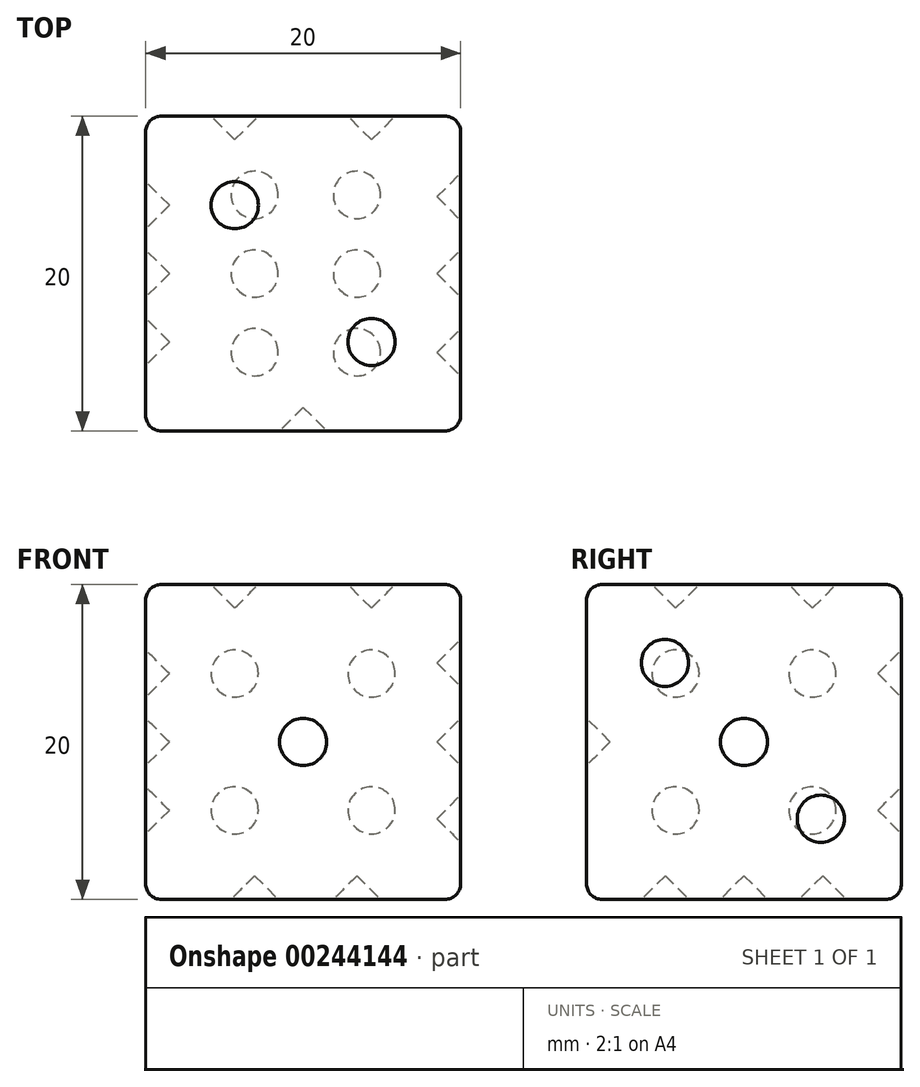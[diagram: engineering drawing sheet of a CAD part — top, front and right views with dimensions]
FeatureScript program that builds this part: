
annotation { "Feature Type Name" : "Feature", "Feature Type Description" : "" }
export const myFeature = defineFeature(function(context is Context, id is Id, definition is map)
    precondition{}
    {
        {
            var Q0;
            Q0=qCreatedBy(makeId("Top.planeOp"),FACE);
            var sketch = newSketch(context, id + "F0", { "sketchPlane" : qUnion([Q0])});
            skLineSegment(sketch, "E0.bottom", {"start": v(0, 0) * mm, "end": v(20, 0) * mm});
            skLineSegment(sketch, "E0.top", {"start": v(0, 20) * mm, "end": v(20, 20) * mm});
            skLineSegment(sketch, "E0.left", {"start": v(0, 0) * mm, "end": v(0, 20) * mm});
            skLineSegment(sketch, "E0.right", {"start": v(20, 0) * mm, "end": v(20, 20) * mm});
            skSolve(sketch);
        }
        {
            var Q0;
            Q0 = qSketchRegion(id + "F0", true);
            extrude(context, id + "F1", {"entities" : qUnion([Q0]), "depth" : 20 * mm});
        }
        {
            var Q0;
            Q0=makeQuery(id+"F1.opExtrude","SWEPT_FACE",FACE,{"disambiguationData":[OSD([sQuery(id+"F0.wireOp",EDGE,"E0.bottom")])]});
            var sketch = newSketch(context, id + "F2", { "sketchPlane" : qUnion([Q0])});
            skLineSegment(sketch, "E1", {"start": v(10, 20) * mm, "end": v(10, 0) * mm, "construction": true});
            skCircle(sketch, "E2", {"center": v(10, 10) * mm, "radius": 1.5 * mm});
            skSolve(sketch);
        }
        {
            var Q0;
            Q0 = qSketchRegion(id + "F2", true);
            extrude(context, id + "F3", {"entities" : qUnion([Q0]), "operationType" : NewBodyOperationType.REMOVE, "oppositeDirection" : true, "depth" : 1.5 * mm});
        }
        {
            var Q0;
            Q0=makeQuery(id+"F1.opExtrude","CAP_EDGE",EDGE,{"disambiguationData":[OSD([sQuery(id+"F0.wireOp",EDGE,"E0.left")])],"isStart":false});
            var Q1;
            Q1=makeQuery(id+"F1.opExtrude","CAP_EDGE",EDGE,{"disambiguationData":[OSD([sQuery(id+"F0.wireOp",EDGE,"E0.right")])],"isStart":false});
            var Q2;
            Q2=makeQuery(id+"F1.opExtrude","CAP_EDGE",EDGE,{"disambiguationData":[OSD([sQuery(id+"F0.wireOp",EDGE,"E0.right")])],"isStart":true});
            var Q3;
            Q3=makeQuery(id+"F1.opExtrude","CAP_EDGE",EDGE,{"disambiguationData":[OSD([sQuery(id+"F0.wireOp",EDGE,"E0.left")])],"isStart":true});
            var Q4;
            Q4=makeQuery(id+"F1.opExtrude","SWEPT_EDGE",EDGE,{"disambiguationData":[OSD([sQuery(id+"F0.wireOp",EDGE,"E0.bottom"),sQuery(id+"F0.wireOp",EDGE,"E0.left")])]});
            var Q5;
            Q5=makeQuery(id+"F1.opExtrude","SWEPT_EDGE",EDGE,{"disambiguationData":[OSD([sQuery(id+"F0.wireOp",EDGE,"E0.bottom"),sQuery(id+"F0.wireOp",EDGE,"E0.right")])]});
            var Q6;
            Q6=makeQuery(id+"F1.opExtrude","SWEPT_EDGE",EDGE,{"disambiguationData":[OSD([sQuery(id+"F0.wireOp",EDGE,"E0.top"),sQuery(id+"F0.wireOp",EDGE,"E0.right")])]});
            var Q7;
            Q7=makeQuery(id+"F1.opExtrude","CAP_EDGE",EDGE,{"disambiguationData":[OSD([sQuery(id+"F0.wireOp",EDGE,"E0.top")])],"isStart":false});
            var Q8;
            Q8=makeQuery(id+"F1.opExtrude","SWEPT_EDGE",EDGE,{"disambiguationData":[OSD([sQuery(id+"F0.wireOp",EDGE,"E0.top"),sQuery(id+"F0.wireOp",EDGE,"E0.left")])]});
            var Q9;
            Q9=makeQuery(id+"F1.opExtrude","CAP_EDGE",EDGE,{"disambiguationData":[OSD([sQuery(id+"F0.wireOp",EDGE,"E0.bottom")])],"isStart":true});
            var Q10;
            Q10=makeQuery(id+"F1.opExtrude","CAP_EDGE",EDGE,{"disambiguationData":[OSD([sQuery(id+"F0.wireOp",EDGE,"E0.top")])],"isStart":true});
            var Q11;
            Q11=makeQuery(id+"F1.opExtrude","SWEPT_FACE",FACE,{"disambiguationData":[OSD([sQuery(id+"F0.wireOp",EDGE,"E0.right")])]});
            var Q12;
            Q12=makeQuery(id+"F1.opExtrude","CAP_EDGE",EDGE,{"disambiguationData":[OSD([sQuery(id+"F0.wireOp",EDGE,"E0.bottom")])],"isStart":false});
            fillet(context, id + "F4", {"entities" : qUnion([Q0, Q1, Q2, Q3, Q4, Q5, Q6, Q7, Q8, Q9, Q10, Q11, Q12]), "radius" : 1 * mm, "tangentPropagation" : true, "allowEdgeOverflow" : false});
        }
        {
            var Q0;
            Q0=makeQuery(id+"F3.boolean.opBoolean","COPY",EDGE,{"derivedFrom":makeQuery(id+"F3.opExtrude","CAP_EDGE",EDGE,{"disambiguationData":[OSD([sQuery(id+"F2.wireOp",EDGE,"E2")])],"isStart":false})});
            chamfer(context, id + "F5", {"entities" : qUnion([Q0]), "width" : 1.5 * mm, "tangentPropagation" : true});
        }
        {
            var Q0;
            Q0=makeQuery(id+"F1.opExtrude","SWEPT_FACE",FACE,{"disambiguationData":[OSD([sQuery(id+"F0.wireOp",EDGE,"E0.right")])]});
            var sketch = newSketch(context, id + "F6", { "sketchPlane" : qUnion([Q0])});
            skCircle(sketch, "E3", {"center": v(4.98, 15.02) * mm, "radius": 1.5 * mm});
            skCircle(sketch, "E4", {"center": v(10, 10) * mm, "radius": 1.5 * mm});
            skCircle(sketch, "E5", {"center": v(14.88, 5.12) * mm, "radius": 1.5 * mm});
            skSolve(sketch);
        }
        {
            var Q0;
            Q0=makeQuery(id+"F1.opExtrude","SWEPT_FACE",FACE,{"disambiguationData":[OSD([sQuery(id+"F0.wireOp",EDGE,"E0.top")])]});
            var sketch = newSketch(context, id + "F7", { "sketchPlane" : qUnion([Q0])});
            skCircle(sketch, "E6", {"center": v(-14.34, 5.66) * mm, "radius": 1.5 * mm});
            skCircle(sketch, "E7", {"center": v(-5.66, 5.66) * mm, "radius": 1.5 * mm});
            skCircle(sketch, "E8", {"center": v(-5.66, 14.34) * mm, "radius": 1.5 * mm});
            skCircle(sketch, "E9", {"center": v(-14.34, 14.34) * mm, "radius": 1.5 * mm});
            skSolve(sketch);
        }
        {
            var Q0;
            Q0=makeQuery(id+"F1.opExtrude","CAP_FACE",FACE,{"disambiguationData":[OSD([sQuery(id+"F0.wireOp",EDGE,"E0.bottom"),sQuery(id+"F0.wireOp",EDGE,"E0.top"),sQuery(id+"F0.wireOp",EDGE,"E0.left"),sQuery(id+"F0.wireOp",EDGE,"E0.right")])],"isStart":true});
            var sketch = newSketch(context, id + "F8", { "sketchPlane" : qUnion([Q0])});
            skCircle(sketch, "E10", {"center": v(6.92, -5) * mm, "radius": 1.5 * mm});
            skCircle(sketch, "E11", {"center": v(6.92, -10) * mm, "radius": 1.5 * mm});
            skCircle(sketch, "E12", {"center": v(6.92, -15) * mm, "radius": 1.5 * mm});
            skCircle(sketch, "E13", {"center": v(13.41, -15) * mm, "radius": 1.5 * mm});
            skCircle(sketch, "E14", {"center": v(13.41, -10) * mm, "radius": 1.5 * mm});
            skCircle(sketch, "E15", {"center": v(13.41, -5) * mm, "radius": 1.5 * mm});
            skSolve(sketch);
        }
        {
            var Q0;
            Q0=makeQuery(id+"F1.opExtrude","SWEPT_FACE",FACE,{"disambiguationData":[OSD([sQuery(id+"F0.wireOp",EDGE,"E0.left")])]});
            var sketch = newSketch(context, id + "F9", { "sketchPlane" : qUnion([Q0])});
            skCircle(sketch, "E16", {"center": v(-10, 10) * mm, "radius": 1.5 * mm});
            skCircle(sketch, "E17", {"center": v(-14.34, 14.34) * mm, "radius": 1.5 * mm});
            skCircle(sketch, "E18", {"center": v(-14.34, 5.66) * mm, "radius": 1.5 * mm});
            skCircle(sketch, "E19", {"center": v(-5.66, 5.66) * mm, "radius": 1.5 * mm});
            skCircle(sketch, "E20", {"center": v(-5.66, 14.34) * mm, "radius": 1.5 * mm});
            skSolve(sketch);
        }
        {
            var Q0;
            Q0=makeQuery(id+"F9.imprint","IMPRINT",FACE,{"disambiguationData":[TD([[makeQuery(id+"F9.imprint","IMPRINT",EDGE,{"derivedFrom":sQuery(id+"F9.wireOp",EDGE,"E20")}),1.0]])]});
            var Q1;
            Q1=makeQuery(id+"F9.imprint","IMPRINT",FACE,{"disambiguationData":[TD([[makeQuery(id+"F9.imprint","IMPRINT",EDGE,{"derivedFrom":sQuery(id+"F9.wireOp",EDGE,"E16")}),1.0]])]});
            var Q2;
            Q2=makeQuery(id+"F9.imprint","IMPRINT",FACE,{"disambiguationData":[TD([[makeQuery(id+"F9.imprint","IMPRINT",EDGE,{"derivedFrom":sQuery(id+"F9.wireOp",EDGE,"E18")}),1.0]])]});
            var Q3;
            Q3=makeQuery(id+"F9.imprint","IMPRINT",FACE,{"disambiguationData":[TD([[makeQuery(id+"F9.imprint","IMPRINT",EDGE,{"derivedFrom":sQuery(id+"F9.wireOp",EDGE,"E19")}),1.0]])]});
            var Q4;
            Q4=makeQuery(id+"F9.imprint","IMPRINT",FACE,{"disambiguationData":[TD([[makeQuery(id+"F9.imprint","IMPRINT",EDGE,{"derivedFrom":sQuery(id+"F9.wireOp",EDGE,"E17")}),1.0]])]});
            var Q5;
            Q5=sQuery(id+"F9.wireOp",EDGE,"E19");
            var Q6;
            Q6=sQuery(id+"F9.wireOp",EDGE,"E16");
            var Q7;
            Q7=sQuery(id+"F9.wireOp",EDGE,"E18");
            var Q8;
            Q8=sQuery(id+"F9.wireOp",EDGE,"E17");
            var Q9;
            Q9=sQuery(id+"F9.wireOp",EDGE,"E20");
            extrude(context, id + "F10", {"entities" : qUnion([Q0, Q1, Q2, Q3, Q4]), "operationType" : NewBodyOperationType.REMOVE, "surfaceEntities" : qUnion([Q5, Q6, Q7, Q8, Q9]), "oppositeDirection" : true, "depth" : 1.5 * mm});
        }
        {
            var Q0;
            Q0=makeQuery(id+"F10.boolean.opBoolean","COPY",FACE,{"derivedFrom":makeQuery(id+"F10.opExtrude","CAP_FACE",FACE,{"disambiguationData":[OSD([sQuery(id+"F9.wireOp",EDGE,"E16")])],"isStart":false})});
            var Q1;
            Q1=makeQuery(id+"F10.boolean.opBoolean","COPY",FACE,{"derivedFrom":makeQuery(id+"F10.opExtrude","CAP_FACE",FACE,{"disambiguationData":[OSD([sQuery(id+"F9.wireOp",EDGE,"E18")])],"isStart":false})});
            var Q2;
            Q2=makeQuery(id+"F10.boolean.opBoolean","COPY",FACE,{"derivedFrom":makeQuery(id+"F10.opExtrude","CAP_FACE",FACE,{"disambiguationData":[OSD([sQuery(id+"F9.wireOp",EDGE,"E17")])],"isStart":false})});
            var Q3;
            Q3=makeQuery(id+"F10.boolean.opBoolean","COPY",FACE,{"derivedFrom":makeQuery(id+"F10.opExtrude","CAP_FACE",FACE,{"disambiguationData":[OSD([sQuery(id+"F9.wireOp",EDGE,"E20")])],"isStart":false})});
            var Q4;
            Q4=makeQuery(id+"F10.boolean.opBoolean","COPY",FACE,{"derivedFrom":makeQuery(id+"F10.opExtrude","CAP_FACE",FACE,{"disambiguationData":[OSD([sQuery(id+"F9.wireOp",EDGE,"E19")])],"isStart":false})});
            chamfer(context, id + "F11", {"entities" : qUnion([Q0, Q1, Q2, Q3, Q4]), "width" : 1.5 * mm, "tangentPropagation" : true});
        }
        {
            var Q0;
            Q0=makeQuery(id+"F8.imprint","IMPRINT",FACE,{"disambiguationData":[TD([[makeQuery(id+"F8.imprint","IMPRINT",EDGE,{"derivedFrom":sQuery(id+"F8.wireOp",EDGE,"E10")}),1.0]])]});
            var Q1;
            Q1=makeQuery(id+"F8.imprint","IMPRINT",FACE,{"disambiguationData":[TD([[makeQuery(id+"F8.imprint","IMPRINT",EDGE,{"derivedFrom":sQuery(id+"F8.wireOp",EDGE,"E15")}),1.0]])]});
            var Q2;
            Q2=makeQuery(id+"F8.imprint","IMPRINT",FACE,{"disambiguationData":[TD([[makeQuery(id+"F8.imprint","IMPRINT",EDGE,{"derivedFrom":sQuery(id+"F8.wireOp",EDGE,"E11")}),1.0]])]});
            var Q3;
            Q3=makeQuery(id+"F8.imprint","IMPRINT",FACE,{"disambiguationData":[TD([[makeQuery(id+"F8.imprint","IMPRINT",EDGE,{"derivedFrom":sQuery(id+"F8.wireOp",EDGE,"E14")}),1.0]])]});
            var Q4;
            Q4=makeQuery(id+"F8.imprint","IMPRINT",FACE,{"disambiguationData":[TD([[makeQuery(id+"F8.imprint","IMPRINT",EDGE,{"derivedFrom":sQuery(id+"F8.wireOp",EDGE,"E12")}),1.0]])]});
            var Q5;
            Q5=makeQuery(id+"F8.imprint","IMPRINT",FACE,{"disambiguationData":[TD([[makeQuery(id+"F8.imprint","IMPRINT",EDGE,{"derivedFrom":sQuery(id+"F8.wireOp",EDGE,"E13")}),1.0]])]});
            var Q6;
            Q6=sQuery(id+"F8.wireOp",EDGE,"E10");
            var Q7;
            Q7=sQuery(id+"F8.wireOp",EDGE,"E15");
            var Q8;
            Q8=sQuery(id+"F8.wireOp",EDGE,"E11");
            var Q9;
            Q9=sQuery(id+"F8.wireOp",EDGE,"E14");
            var Q10;
            Q10=sQuery(id+"F8.wireOp",EDGE,"E13");
            var Q11;
            Q11=sQuery(id+"F8.wireOp",EDGE,"E12");
            extrude(context, id + "F12", {"entities" : qUnion([Q0, Q1, Q2, Q3, Q4, Q5]), "operationType" : NewBodyOperationType.REMOVE, "surfaceEntities" : qUnion([Q6, Q7, Q8, Q9, Q10, Q11]), "oppositeDirection" : true, "depth" : 1.5 * mm});
        }
        {
            var Q0;
            Q0=makeQuery(id+"F12.boolean.opBoolean","COPY",FACE,{"derivedFrom":makeQuery(id+"F12.opExtrude","CAP_FACE",FACE,{"disambiguationData":[OSD([sQuery(id+"F8.wireOp",EDGE,"E10")])],"isStart":false})});
            var Q1;
            Q1=makeQuery(id+"F12.boolean.opBoolean","COPY",FACE,{"derivedFrom":makeQuery(id+"F12.opExtrude","CAP_FACE",FACE,{"disambiguationData":[OSD([sQuery(id+"F8.wireOp",EDGE,"E15")])],"isStart":false})});
            var Q2;
            Q2=makeQuery(id+"F12.boolean.opBoolean","COPY",FACE,{"derivedFrom":makeQuery(id+"F12.opExtrude","CAP_FACE",FACE,{"disambiguationData":[OSD([sQuery(id+"F8.wireOp",EDGE,"E11")])],"isStart":false})});
            var Q3;
            Q3=makeQuery(id+"F12.boolean.opBoolean","COPY",FACE,{"derivedFrom":makeQuery(id+"F12.opExtrude","CAP_FACE",FACE,{"disambiguationData":[OSD([sQuery(id+"F8.wireOp",EDGE,"E14")])],"isStart":false})});
            var Q4;
            Q4=makeQuery(id+"F12.boolean.opBoolean","COPY",FACE,{"derivedFrom":makeQuery(id+"F12.opExtrude","CAP_FACE",FACE,{"disambiguationData":[OSD([sQuery(id+"F8.wireOp",EDGE,"E13")])],"isStart":false})});
            var Q5;
            Q5=makeQuery(id+"F12.boolean.opBoolean","COPY",FACE,{"derivedFrom":makeQuery(id+"F12.opExtrude","CAP_FACE",FACE,{"disambiguationData":[OSD([sQuery(id+"F8.wireOp",EDGE,"E12")])],"isStart":false})});
            chamfer(context, id + "F13", {"entities" : qUnion([Q0, Q1, Q2, Q3, Q4, Q5]), "width" : 1.5 * mm, "tangentPropagation" : true});
        }
        {
            var Q0;
            Q0=makeQuery(id+"F6.imprint","IMPRINT",FACE,{"disambiguationData":[TD([[makeQuery(id+"F6.imprint","IMPRINT",EDGE,{"derivedFrom":sQuery(id+"F6.wireOp",EDGE,"E3")}),1.0]])]});
            var Q1;
            Q1=makeQuery(id+"F6.imprint","IMPRINT",FACE,{"disambiguationData":[TD([[makeQuery(id+"F6.imprint","IMPRINT",EDGE,{"derivedFrom":sQuery(id+"F6.wireOp",EDGE,"E4")}),1.0]])]});
            var Q2;
            Q2=makeQuery(id+"F6.imprint","IMPRINT",FACE,{"disambiguationData":[TD([[makeQuery(id+"F6.imprint","IMPRINT",EDGE,{"derivedFrom":sQuery(id+"F6.wireOp",EDGE,"E5")}),1.0]])]});
            var Q3;
            Q3=sQuery(id+"F6.wireOp",EDGE,"E3");
            var Q4;
            Q4=sQuery(id+"F6.wireOp",EDGE,"E4");
            var Q5;
            Q5=sQuery(id+"F6.wireOp",EDGE,"E5");
            extrude(context, id + "F14", {"entities" : qUnion([Q0, Q1, Q2]), "operationType" : NewBodyOperationType.REMOVE, "surfaceEntities" : qUnion([Q3, Q4, Q5]), "oppositeDirection" : true, "depth" : 1.5 * mm});
        }
        {
            var Q0;
            Q0=makeQuery(id+"F14.boolean.opBoolean","COPY",FACE,{"derivedFrom":makeQuery(id+"F14.opExtrude","CAP_FACE",FACE,{"disambiguationData":[OSD([sQuery(id+"F6.wireOp",EDGE,"E3")])],"isStart":false})});
            var Q1;
            Q1=makeQuery(id+"F14.boolean.opBoolean","COPY",FACE,{"derivedFrom":makeQuery(id+"F14.opExtrude","CAP_FACE",FACE,{"disambiguationData":[OSD([sQuery(id+"F6.wireOp",EDGE,"E4")])],"isStart":false})});
            var Q2;
            Q2=makeQuery(id+"F14.boolean.opBoolean","COPY",FACE,{"derivedFrom":makeQuery(id+"F14.opExtrude","CAP_FACE",FACE,{"disambiguationData":[OSD([sQuery(id+"F6.wireOp",EDGE,"E5")])],"isStart":false})});
            chamfer(context, id + "F15", {"entities" : qUnion([Q0, Q1, Q2]), "width" : 1.5 * mm, "tangentPropagation" : true});
        }
        {
            var Q0;
            Q0=makeQuery(id+"F7.imprint","IMPRINT",FACE,{"disambiguationData":[TD([[makeQuery(id+"F7.imprint","IMPRINT",EDGE,{"derivedFrom":sQuery(id+"F7.wireOp",EDGE,"E9")}),1.0]])]});
            var Q1;
            Q1=makeQuery(id+"F7.imprint","IMPRINT",FACE,{"disambiguationData":[TD([[makeQuery(id+"F7.imprint","IMPRINT",EDGE,{"derivedFrom":sQuery(id+"F7.wireOp",EDGE,"E8")}),1.0]])]});
            var Q2;
            Q2=makeQuery(id+"F7.imprint","IMPRINT",FACE,{"disambiguationData":[TD([[makeQuery(id+"F7.imprint","IMPRINT",EDGE,{"derivedFrom":sQuery(id+"F7.wireOp",EDGE,"E6")}),1.0]])]});
            var Q3;
            Q3=makeQuery(id+"F7.imprint","IMPRINT",FACE,{"disambiguationData":[TD([[makeQuery(id+"F7.imprint","IMPRINT",EDGE,{"derivedFrom":sQuery(id+"F7.wireOp",EDGE,"E7")}),1.0]])]});
            extrude(context, id + "F16", {"entities" : qUnion([Q0, Q1, Q2, Q3]), "operationType" : NewBodyOperationType.REMOVE, "oppositeDirection" : true, "depth" : 1.5 * mm});
        }
        {
            var Q0;
            Q0=makeQuery(id+"F16.boolean.opBoolean","COPY",FACE,{"derivedFrom":makeQuery(id+"F16.opExtrude","CAP_FACE",FACE,{"disambiguationData":[OSD([sQuery(id+"F7.wireOp",EDGE,"E9")])],"isStart":false})});
            var Q1;
            Q1=makeQuery(id+"F16.boolean.opBoolean","COPY",FACE,{"derivedFrom":makeQuery(id+"F16.opExtrude","CAP_FACE",FACE,{"disambiguationData":[OSD([sQuery(id+"F7.wireOp",EDGE,"E8")])],"isStart":false})});
            var Q2;
            Q2=makeQuery(id+"F16.boolean.opBoolean","COPY",FACE,{"derivedFrom":makeQuery(id+"F16.opExtrude","CAP_FACE",FACE,{"disambiguationData":[OSD([sQuery(id+"F7.wireOp",EDGE,"E7")])],"isStart":false})});
            var Q3;
            Q3=makeQuery(id+"F16.boolean.opBoolean","COPY",FACE,{"derivedFrom":makeQuery(id+"F16.opExtrude","CAP_FACE",FACE,{"disambiguationData":[OSD([sQuery(id+"F7.wireOp",EDGE,"E6")])],"isStart":false})});
            chamfer(context, id + "F17", {"entities" : qUnion([Q0, Q1, Q2, Q3]), "width" : 1.5 * mm, "tangentPropagation" : true});
        }
        {
            var Q0;
            Q0=makeQuery(id+"F1.opExtrude","CAP_FACE",FACE,{"disambiguationData":[OSD([sQuery(id+"F0.wireOp",EDGE,"E0.bottom"),sQuery(id+"F0.wireOp",EDGE,"E0.top"),sQuery(id+"F0.wireOp",EDGE,"E0.left"),sQuery(id+"F0.wireOp",EDGE,"E0.right")])],"isStart":false});
            var sketch = newSketch(context, id + "F18", { "sketchPlane" : qUnion([Q0])});
            skCircle(sketch, "E21", {"center": v(5.66, 14.34) * mm, "radius": 1.5 * mm});
            skCircle(sketch, "E22", {"center": v(14.34, 5.66) * mm, "radius": 1.5 * mm});
            skSolve(sketch);
        }
        {
            var Q0;
            Q0=makeQuery(id+"F18.imprint","IMPRINT",FACE,{"disambiguationData":[TD([[makeQuery(id+"F18.imprint","IMPRINT",EDGE,{"derivedFrom":sQuery(id+"F18.wireOp",EDGE,"E21")}),1.0]])]});
            var Q1;
            Q1=makeQuery(id+"F18.imprint","IMPRINT",FACE,{"disambiguationData":[TD([[makeQuery(id+"F18.imprint","IMPRINT",EDGE,{"derivedFrom":sQuery(id+"F18.wireOp",EDGE,"E22")}),1.0]])]});
            var Q2;
            Q2=sQuery(id+"F18.wireOp",EDGE,"E21");
            var Q3;
            Q3=sQuery(id+"F18.wireOp",EDGE,"E22");
            extrude(context, id + "F19", {"entities" : qUnion([Q0, Q1]), "operationType" : NewBodyOperationType.REMOVE, "surfaceEntities" : qUnion([Q2, Q3]), "oppositeDirection" : true, "depth" : 1.5 * mm});
        }
        {
            var Q0;
            Q0=makeQuery(id+"F19.boolean.opBoolean","COPY",EDGE,{"derivedFrom":makeQuery(id+"F19.opExtrude","CAP_EDGE",EDGE,{"disambiguationData":[OSD([sQuery(id+"F18.wireOp",EDGE,"E21")])],"isStart":false})});
            var Q1;
            Q1=makeQuery(id+"F19.boolean.opBoolean","COPY",EDGE,{"derivedFrom":makeQuery(id+"F19.opExtrude","CAP_EDGE",EDGE,{"disambiguationData":[OSD([sQuery(id+"F18.wireOp",EDGE,"E22")])],"isStart":false})});
            chamfer(context, id + "F20", {"entities" : qUnion([Q0, Q1]), "width" : 1.5 * mm, "tangentPropagation" : true});
        }
    });
